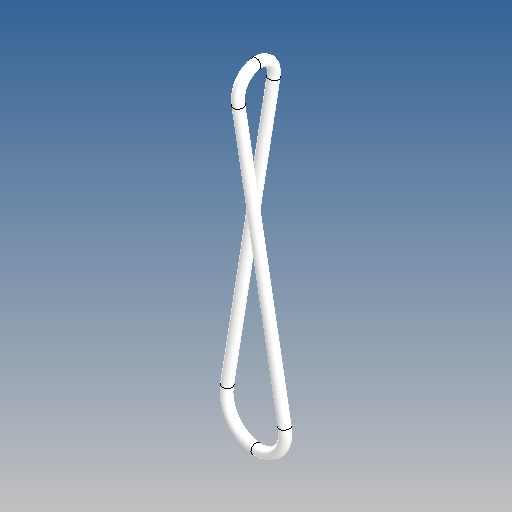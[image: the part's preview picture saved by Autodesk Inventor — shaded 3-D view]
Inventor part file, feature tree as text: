
AUTODESK INVENTOR PART (.ipt)
format: ipt  version: 2025.1 (Build 291241000, 241)  size: 166,912 bytes
history: native  units: mm
features: other x9, sketch x2, loft x2, plane x1
ambient origin geometry x8: Origin, YZ Plane, XZ Plane, XY Plane, X Axis, Y Axis, Z Axis, Center Point
bodies: Volumenkörper1 (feature_tree)
feature tree (14):
  plane  "Arbeitsebene1"
  other  "Arbeitsachse3"
  sketch  "Skizze1"  dims[d0=27.8077mm d3=1.0mm]
  sketch  "Skizze2"  dims[d4=3.3mm d5=1.5mm d6=10.0mm d7=2.7mm d8=0.0mm d9=90.0deg d10=90.0deg d11=0.0mm d12=0.0mm d13=1.5mm d14=10.0mm d15=2.7mm d16=0.0mm d17=90.0deg d18=90.0deg d19=0.0mm d20=0.0mm d21=2.1mm d22=1.0mm d23=1.25mm d24=10.0mm d25=2.7mm d26=0.0mm d27=90.0deg d28=90.0deg d29=0.0mm d30=0.0mm d31=1.25mm d32=10.0mm d33=2.7mm d34=0.0mm d35=90.0deg d36=90.0deg d37=0.0mm d38=0.0mm d39=0.0mm d40=90.0deg d41=0.0mm d42=90.0deg d43=0.0mm d44=90.0deg d45=0.0mm d46=90.0deg]
  other  "Spirale1"
  other  "Spirale2"
  other  "Spirale3"
  other  "Spirale4"
  loft  "Erhebung1"
  loft  "Erhebung2"
  other  "Kanten1"
  other  "Kanten2"
  other  "Kanten3"
  other  "Kanten4"
